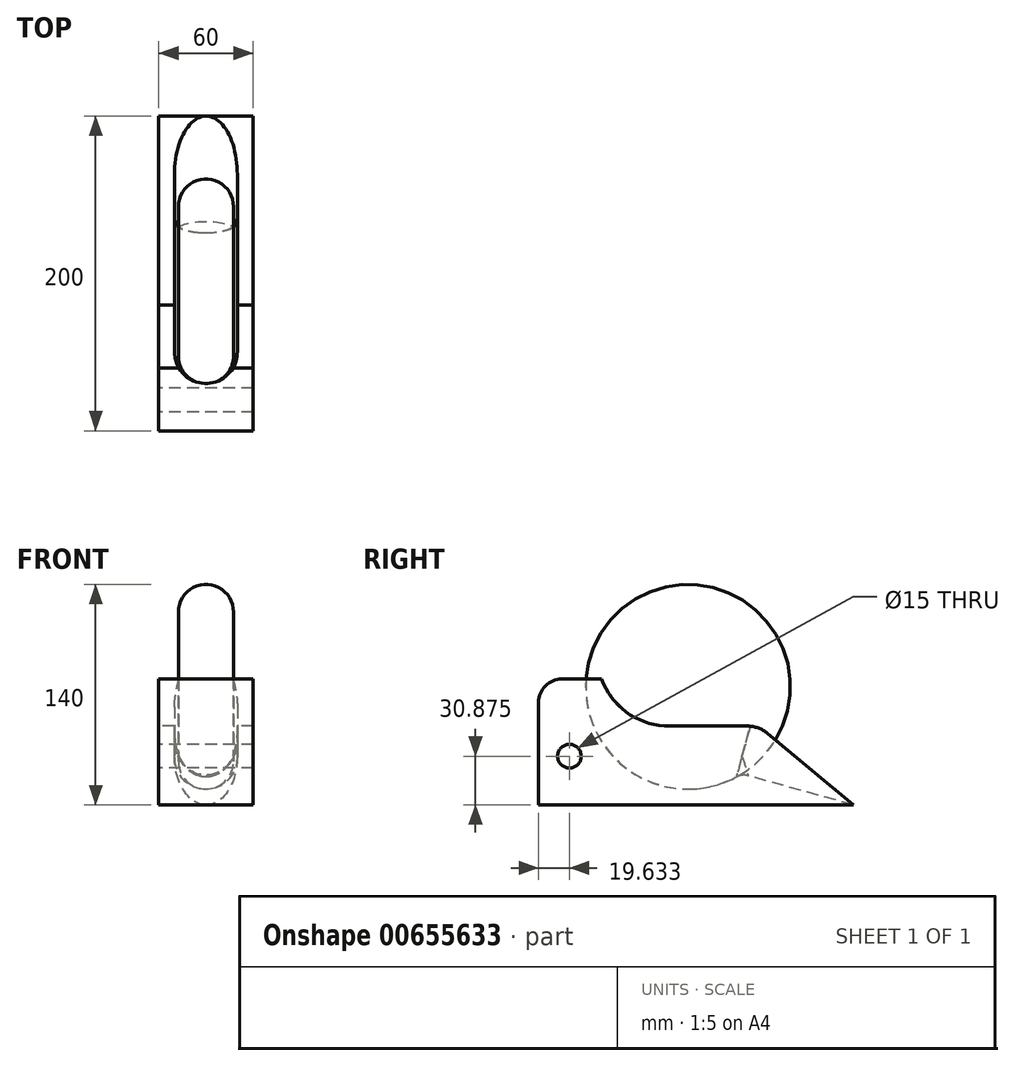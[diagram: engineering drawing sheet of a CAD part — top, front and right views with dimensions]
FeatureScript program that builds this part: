
annotation { "Feature Type Name" : "Feature", "Feature Type Description" : "" }
export const myFeature = defineFeature(function(context is Context, id is Id, definition is map)
    precondition{}
    {
        {
            var Q0;
            Q0=qCreatedBy(makeId("Right.planeOp"),FACE);
            var sketch = newSketch(context, id + "F0", { "sketchPlane" : qUnion([Q0])});
            skLineSegment(sketch, "E0", {"start": v(0, 0) * mm, "end": v(-100, 0) * mm});
            skLineSegment(sketch, "E1", {"start": v(0, 0) * mm, "end": v(100, 0) * mm});
            skLineSegment(sketch, "E2", {"start": v(-100, 0) * mm, "end": v(-100, 80) * mm});
            skLineSegment(sketch, "E3", {"start": v(-100, 80) * mm, "end": v(-60, 80) * mm});
            skLineSegment(sketch, "E4", {"start": v(-60, 80) * mm, "end": v(-60, 50) * mm, "construction": true});
            skLineSegment(sketch, "E5", {"start": v(-60, 50) * mm, "end": v(40, 50) * mm, "construction": true});
            skLineSegment(sketch, "E6", {"start": v(45.56, 45.36) * mm, "end": v(100, 0) * mm});
            skPoint(sketch, "E7", {"position": v(-20, 50) * mm});
            skArc(sketch, "E8", {"start": v(-60, 80) * mm, "mid": v(-44.4, 59.13) * mm, "end": v(-20, 50) * mm});
            skLineSegment(sketch, "E9", {"start": v(-20, 50) * mm, "end": v(32.76, 50) * mm});
            skPoint(sketch, "E10.visualSharp", {"position": v(40, 50) * mm});
            skArc(sketch, "E10.filletArc", {"start": v(45.56, 45.36) * mm, "mid": v(39.57, 48.8) * mm, "end": v(32.76, 50) * mm});
            skPoint(sketch, "E11", {"position": v(-5, 0) * mm});
            skLineSegment(sketch, "E12", {"start": v(-5, 0) * mm, "end": v(-5, 75) * mm, "construction": true});
            skCircle(sketch, "E13", {"center": v(-5, 75) * mm, "radius": 65 * mm});
            skCircle(sketch, "E14", {"center": v(-80.37, 30.87) * mm, "radius": 7.5 * mm});
            skSolve(sketch);
        }
        {
            var Q0;
            {var subQ0=sQuery(id+"F0.wireOp",EDGE,"E8");Q0=makeQuery(id+"F0.imprint","IMPRINT",FACE,{"disambiguationData":[TD([[makeQuery(id+"F0.imprint","IMPRINT",EDGE,{"derivedFrom":subQ0}),1.0]])]});}
            var Q1;
            {var subQ0=sQuery(id+"F0.wireOp",EDGE,"E8");Q1=makeQuery(id+"F0.imprint","IMPRINT",FACE,{"disambiguationData":[TD([[makeQuery(id+"F0.imprint","IMPRINT",EDGE,{"derivedFrom":subQ0}),-1.0]])]});}
            extrude(context, id + "F1", {"entities" : qUnion([Q0, Q1]), "endBound" : BoundingType.SYMMETRIC, "depth" : 35 * mm, "offsetDistance" : 25 * mm});
        }
        {
            var Q0;
            Q0=makeQuery(id+"F1.opExtrude","CAP_EDGE",EDGE,{"disambiguationData":[OSD([sQuery(id+"F0.wireOp",EDGE,"E13")])],"isStart":false});
            var Q1;
            Q1=makeQuery(id+"F1.opExtrude","CAP_EDGE",EDGE,{"disambiguationData":[OSD([sQuery(id+"F0.wireOp",EDGE,"E13")])],"isStart":true});
            fillet(context, id + "F2", {"entities" : qUnion([Q0, Q1]), "radius" : 17.5 * mm, "tangentPropagation" : true, "allowEdgeOverflow" : false});
        }
        {
            var Q0;
            Q0=makeQuery(id+"F0.imprint","IMPRINT",FACE,{"disambiguationData":[TD([[makeQuery(id+"F0.imprint","IMPRINT",EDGE,{"derivedFrom":sQuery(id+"F0.wireOp",EDGE,"E0")}),-1.0]])]});
            var Q1;
            {var subQ0=sQuery(id+"F0.wireOp",EDGE,"E8");Q1=makeQuery(id+"F0.imprint","IMPRINT",FACE,{"disambiguationData":[TD([[makeQuery(id+"F0.imprint","IMPRINT",EDGE,{"derivedFrom":subQ0}),-1.0]])]});}
            extrude(context, id + "F3", {"entities" : qUnion([Q0, Q1]), "endBound" : BoundingType.SYMMETRIC, "depth" : 60 * mm, "offsetDistance" : 25 * mm});
        }
        {
            var Q0;
            {var subQ0=sQuery(id+"F0.wireOp",EDGE,"E8");Q0=makeQuery(id+"F0.imprint","IMPRINT",FACE,{"disambiguationData":[TD([[makeQuery(id+"F0.imprint","IMPRINT",EDGE,{"derivedFrom":subQ0}),1.0]])]});}
            var Q1;
            {var subQ0=sQuery(id+"F0.wireOp",EDGE,"E8");Q1=makeQuery(id+"F0.imprint","IMPRINT",FACE,{"disambiguationData":[TD([[makeQuery(id+"F0.imprint","IMPRINT",EDGE,{"derivedFrom":subQ0}),-1.0]])]});}
            extrude(context, id + "F4", {"entities" : qUnion([Q0, Q1]), "endBound" : BoundingType.SYMMETRIC, "depth" : 40 * mm, "offsetDistance" : 25 * mm});
        }
        {
            var Q0;
            Q0=makeQuery(id+"F4.opExtrude","CAP_EDGE",EDGE,{"disambiguationData":[OSD([sQuery(id+"F0.wireOp",EDGE,"E13")])],"isStart":false});
            var Q1;
            Q1=makeQuery(id+"F4.opExtrude","CAP_EDGE",EDGE,{"disambiguationData":[OSD([sQuery(id+"F0.wireOp",EDGE,"E13")])],"isStart":true});
            fillet(context, id + "F5", {"entities" : qUnion([Q0, Q1]), "radius" : 20 * mm, "tangentPropagation" : true, "allowEdgeOverflow" : false});
        }
        {
            var Q0;
            Q0=makeQuery(id+"F4.opExtrude","SWEPT_BODY",BODY,{"disambiguationData":[OSD([sQuery(id+"F0.wireOp",EDGE,"E13")])]});
            var Q1;
            Q1=makeQuery(id+"F3.opExtrude","SWEPT_BODY",BODY,{"disambiguationData":[OSD([sQuery(id+"F0.wireOp",EDGE,"E0"),sQuery(id+"F0.wireOp",EDGE,"E1"),sQuery(id+"F0.wireOp",EDGE,"E2"),sQuery(id+"F0.wireOp",EDGE,"E3"),sQuery(id+"F0.wireOp",EDGE,"E6"),sQuery(id+"F0.wireOp",EDGE,"E8"),sQuery(id+"F0.wireOp",EDGE,"E9"),sQuery(id+"F0.wireOp",EDGE,"E10.filletArc")])]});
            booleanBodies(context, id + "F6", {"operationType" : BooleanOperationType.SUBTRACTION, "tools" : qUnion([Q0]), "targets" : qUnion([Q1])});
        }
        {
            var Q0;
            Q0=makeQuery(id+"F3.opExtrude","SWEPT_EDGE",EDGE,{"disambiguationData":[OSD([sQuery(id+"F0.wireOp",EDGE,"E2"),sQuery(id+"F0.wireOp",EDGE,"E3")])]});
            fillet(context, id + "F7", {"entities" : qUnion([Q0]), "radius" : 15 * mm, "tangentPropagation" : true, "allowEdgeOverflow" : false});
        }
        {
            var Q0;
            Q0=qCreatedBy(makeId("Right.planeOp"),FACE);
            var sketch = newSketch(context, id + "F8", { "sketchPlane" : qUnion([Q0])});
            skLineSegment(sketch, "E15.0", {"start": v(0, 0) * mm, "end": v(100, 0) * mm});
            skLineSegment(sketch, "E16", {"start": v(100, 0) * mm, "end": v(26.35, 20.41) * mm});
            skLineSegment(sketch, "E17", {"start": v(26.35, 20.41) * mm, "end": v(45.25, 88.63) * mm});
            skLineSegment(sketch, "E18", {"start": v(100, 0) * mm, "end": v(118.9, 68.22) * mm});
            skLineSegment(sketch, "E19", {"start": v(118.9, 68.22) * mm, "end": v(45.25, 88.63) * mm});
            skSolve(sketch);
        }
        {
            var Q0;
            Q0=makeQuery(id+"F8.imprint","IMPRINT",FACE,{"disambiguationData":[TD([[makeQuery(id+"F8.imprint","IMPRINT",EDGE,{"derivedFrom":sQuery(id+"F8.wireOp",EDGE,"E16")}),-1.0]])]});
            extrude(context, id + "F9", {"entities" : qUnion([Q0]), "endBound" : BoundingType.SYMMETRIC, "depth" : 40 * mm, "offsetDistance" : 25 * mm});
        }
        {
            var Q0;
            Q0=makeQuery(id+"F9.opExtrude","CAP_EDGE",EDGE,{"disambiguationData":[OSD([sQuery(id+"F8.wireOp",EDGE,"E16")])],"isStart":false});
            var Q1;
            Q1=makeQuery(id+"F9.opExtrude","CAP_EDGE",EDGE,{"disambiguationData":[OSD([sQuery(id+"F8.wireOp",EDGE,"E16")])],"isStart":true});
            fillet(context, id + "F10", {"entities" : qUnion([Q0, Q1]), "radius" : 20 * mm, "tangentPropagation" : true, "allowEdgeOverflow" : false});
        }
        {
            var Q0;
            Q0=makeQuery(id+"F9.opExtrude","SWEPT_BODY",BODY,{"disambiguationData":[OSD([sQuery(id+"F8.wireOp",EDGE,"E16"),sQuery(id+"F8.wireOp",EDGE,"E17"),sQuery(id+"F8.wireOp",EDGE,"E18"),sQuery(id+"F8.wireOp",EDGE,"E19")])]});
            var Q1;
            Q1=makeQuery(id+"F3.opExtrude","SWEPT_BODY",BODY,{"disambiguationData":[OSD([sQuery(id+"F0.wireOp",EDGE,"E0"),sQuery(id+"F0.wireOp",EDGE,"E1"),sQuery(id+"F0.wireOp",EDGE,"E2"),sQuery(id+"F0.wireOp",EDGE,"E3"),sQuery(id+"F0.wireOp",EDGE,"E6"),sQuery(id+"F0.wireOp",EDGE,"E8"),sQuery(id+"F0.wireOp",EDGE,"E9"),sQuery(id+"F0.wireOp",EDGE,"E10.filletArc"),sQuery(id+"F0.wireOp",EDGE,"E14")])]});
            booleanBodies(context, id + "F11", {"operationType" : BooleanOperationType.SUBTRACTION, "tools" : qUnion([Q0]), "targets" : qUnion([Q1])});
        }
        {
            var Q0;
            Q0=makeQuery(id+"F11.opBoolean","INTERSECT",EDGE,{"derivedFrom":[makeQuery(id+"F6.opBoolean","COPY",FACE,{"derivedFrom":makeQuery(id+"F5.opFillet","BLEND_FACE",FACE,{"disambiguationData":[OSD([sQuery(id+"F0.wireOp",EDGE,"E13")])]})}),makeQuery(id+"F10.opFillet","BLEND_FACE",FACE,{"disambiguationData":[OSD([sQuery(id+"F8.wireOp",EDGE,"E16")])]})]});
            fillet(context, id + "F12", {"entities" : qUnion([Q0]), "radius" : 10 * mm, "tangentPropagation" : true, "allowEdgeOverflow" : false});
        }
    });
